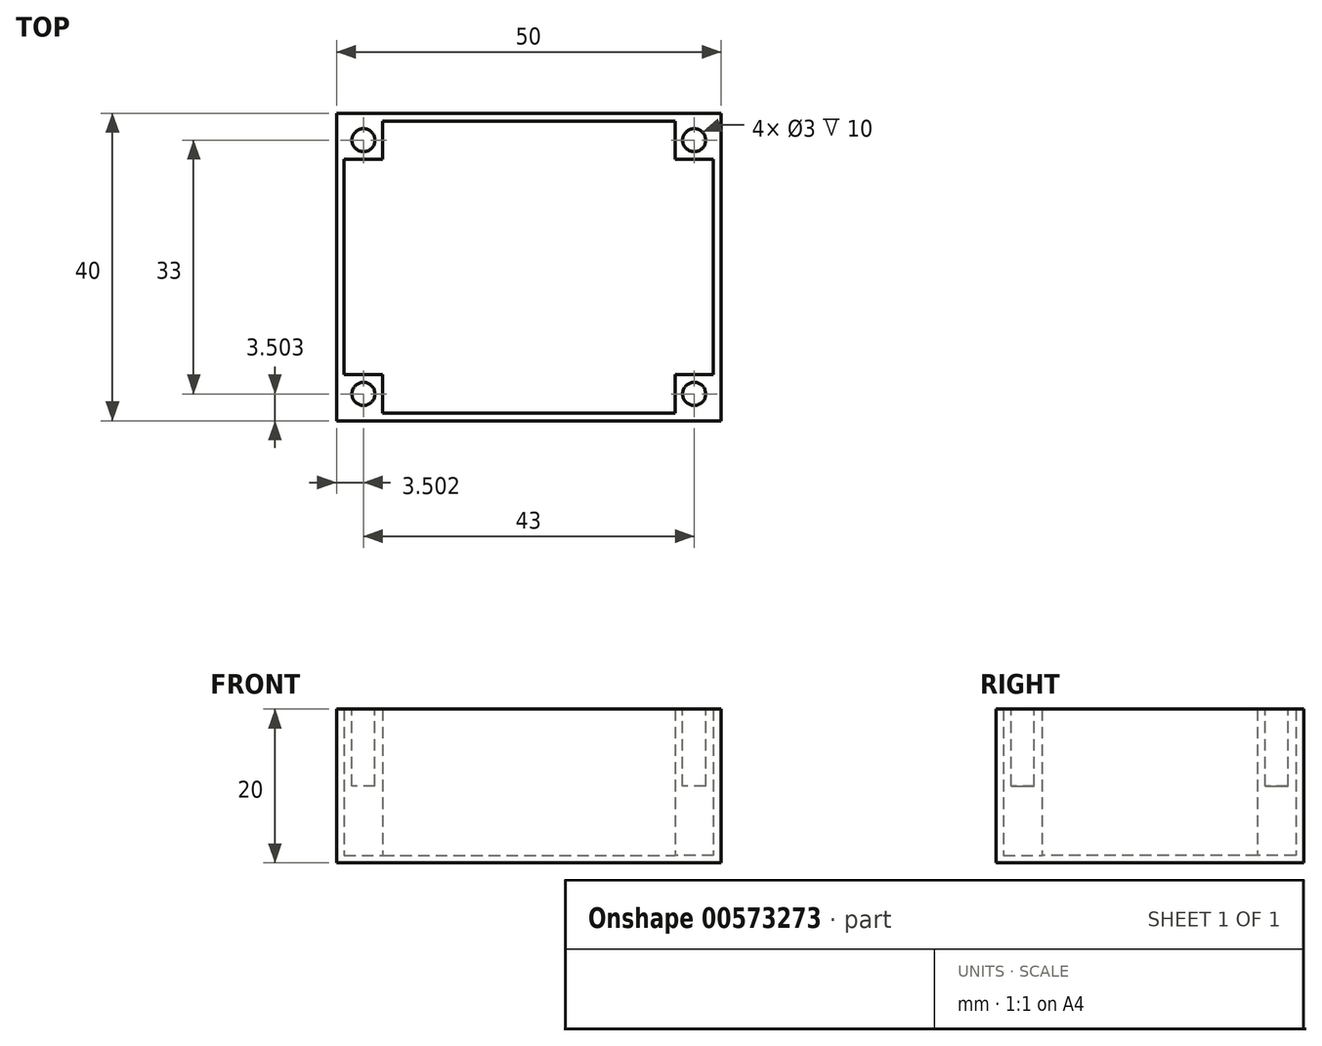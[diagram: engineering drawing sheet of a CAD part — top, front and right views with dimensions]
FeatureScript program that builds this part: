
annotation { "Feature Type Name" : "Feature", "Feature Type Description" : "" }
export const myFeature = defineFeature(function(context is Context, id is Id, definition is map)
    precondition{}
    {
        {
            var Q0;
            Q0=qCreatedBy(makeId("Top.planeOp"),FACE);
            var sketch = newSketch(context, id + "F0", { "sketchPlane" : qUnion([Q0])});
            skLineSegment(sketch, "E0.bottom", {"start": v(-61.69, 57.06) * mm, "end": v(-11.69, 57.06) * mm});
            skLineSegment(sketch, "E0.top", {"start": v(-61.69, 17.06) * mm, "end": v(-11.69, 17.06) * mm});
            skLineSegment(sketch, "E0.left", {"start": v(-61.69, 57.06) * mm, "end": v(-61.69, 17.06) * mm});
            skLineSegment(sketch, "E0.right", {"start": v(-11.69, 57.06) * mm, "end": v(-11.69, 17.06) * mm});
            skSolve(sketch);
        }
        {
            var Q0;
            Q0=makeQuery(id+"F0.imprint","IMPRINT",FACE,{"disambiguationData":[TD([[makeQuery(id+"F0.imprint","IMPRINT",EDGE,{"derivedFrom":sQuery(id+"F0.wireOp",EDGE,"E0.bottom")}),-1.0]])]});
            extrude(context, id + "F1", {"entities" : qUnion([Q0]), "depth" : 20 * mm, "offsetDistance" : 25 * mm});
        }
        {
            var Q0;
            Q0=makeQuery(id+"F1.opExtrude","CAP_FACE",FACE,{"disambiguationData":[OSD([sQuery(id+"F0.wireOp",EDGE,"E0.bottom"),sQuery(id+"F0.wireOp",EDGE,"E0.top"),sQuery(id+"F0.wireOp",EDGE,"E0.left"),sQuery(id+"F0.wireOp",EDGE,"E0.right")])],"isStart":false});
            var sketch = newSketch(context, id + "F2", { "sketchPlane" : qUnion([Q0])});
            skLineSegment(sketch, "E1.bottom", {"start": v(-60.69, 56.06) * mm, "end": v(-12.69, 56.06) * mm});
            skLineSegment(sketch, "E1.top", {"start": v(-60.69, 18.06) * mm, "end": v(-12.69, 18.06) * mm});
            skLineSegment(sketch, "E1.left", {"start": v(-60.69, 56.06) * mm, "end": v(-60.69, 18.06) * mm});
            skLineSegment(sketch, "E1.right", {"start": v(-12.69, 56.06) * mm, "end": v(-12.69, 18.06) * mm});
            skSolve(sketch);
        }
        {
            var Q0;
            Q0=makeQuery(id+"F2.imprint","IMPRINT",FACE,{"disambiguationData":[TD([[makeQuery(id+"F2.imprint","IMPRINT",EDGE,{"derivedFrom":sQuery(id+"F2.wireOp",EDGE,"E1.bottom")}),-1.0]])]});
            extrude(context, id + "F3", {"entities" : qUnion([Q0]), "operationType" : NewBodyOperationType.REMOVE, "oppositeDirection" : true, "depth" : 19 * mm, "offsetDistance" : 25 * mm});
        }
        {
            var Q0;
            Q0=makeQuery(id+"F3.boolean.opBoolean","COPY",FACE,{"derivedFrom":makeQuery(id+"F3.opExtrude","CAP_FACE",FACE,{"disambiguationData":[OSD([sQuery(id+"F2.wireOp",EDGE,"E1.bottom"),sQuery(id+"F2.wireOp",EDGE,"E1.top"),sQuery(id+"F2.wireOp",EDGE,"E1.left"),sQuery(id+"F2.wireOp",EDGE,"E1.right")])],"isStart":false})});
            var sketch = newSketch(context, id + "F4", { "sketchPlane" : qUnion([Q0])});
            skLineSegment(sketch, "E2.bottom", {"start": v(-12.69, 56.06) * mm, "end": v(-17.69, 56.06) * mm});
            skLineSegment(sketch, "E2.top", {"start": v(-12.69, 51.06) * mm, "end": v(-17.69, 51.06) * mm});
            skLineSegment(sketch, "E2.left", {"start": v(-12.69, 56.06) * mm, "end": v(-12.69, 51.06) * mm});
            skLineSegment(sketch, "E2.right", {"start": v(-17.69, 56.06) * mm, "end": v(-17.69, 51.06) * mm});
            skLineSegment(sketch, "E3.bottom", {"start": v(-12.69, 18.06) * mm, "end": v(-17.69, 18.06) * mm});
            skLineSegment(sketch, "E3.top", {"start": v(-12.69, 23.06) * mm, "end": v(-17.69, 23.06) * mm});
            skLineSegment(sketch, "E3.left", {"start": v(-12.69, 18.06) * mm, "end": v(-12.69, 23.06) * mm});
            skLineSegment(sketch, "E3.right", {"start": v(-17.69, 18.06) * mm, "end": v(-17.69, 23.06) * mm});
            skLineSegment(sketch, "E4.bottom", {"start": v(-60.69, 56.06) * mm, "end": v(-55.69, 56.06) * mm});
            skLineSegment(sketch, "E4.top", {"start": v(-60.69, 51.06) * mm, "end": v(-55.69, 51.06) * mm});
            skLineSegment(sketch, "E4.left", {"start": v(-60.69, 56.06) * mm, "end": v(-60.69, 51.06) * mm});
            skLineSegment(sketch, "E4.right", {"start": v(-55.69, 56.06) * mm, "end": v(-55.69, 51.06) * mm});
            skLineSegment(sketch, "E5.bottom", {"start": v(-60.69, 18.06) * mm, "end": v(-55.69, 18.06) * mm});
            skLineSegment(sketch, "E5.top", {"start": v(-60.69, 23.06) * mm, "end": v(-55.69, 23.06) * mm});
            skLineSegment(sketch, "E5.left", {"start": v(-60.69, 18.06) * mm, "end": v(-60.69, 23.06) * mm});
            skLineSegment(sketch, "E5.right", {"start": v(-55.69, 18.06) * mm, "end": v(-55.69, 23.06) * mm});
            skSolve(sketch);
        }
        {
            var Q0;
            Q0=makeQuery(id+"F4.imprint","IMPRINT",FACE,{"disambiguationData":[TD([[makeQuery(id+"F4.imprint","IMPRINT",EDGE,{"derivedFrom":sQuery(id+"F4.wireOp",EDGE,"E2.bottom")}),-1.0]])]});
            var Q1;
            Q1=makeQuery(id+"F4.imprint","IMPRINT",FACE,{"disambiguationData":[TD([[makeQuery(id+"F4.imprint","IMPRINT",EDGE,{"derivedFrom":sQuery(id+"F4.wireOp",EDGE,"E3.bottom")}),1.0]])]});
            var Q2;
            Q2=makeQuery(id+"F4.imprint","IMPRINT",FACE,{"disambiguationData":[TD([[makeQuery(id+"F4.imprint","IMPRINT",EDGE,{"derivedFrom":sQuery(id+"F4.wireOp",EDGE,"E5.bottom")}),1.0]])]});
            var Q3;
            Q3=makeQuery(id+"F4.imprint","IMPRINT",FACE,{"disambiguationData":[TD([[makeQuery(id+"F4.imprint","IMPRINT",EDGE,{"derivedFrom":sQuery(id+"F4.wireOp",EDGE,"E4.bottom")}),-1.0]])]});
            extrude(context, id + "F5", {"entities" : qUnion([Q0, Q1, Q2, Q3]), "operationType" : NewBodyOperationType.ADD, "depth" : 19 * mm, "offsetDistance" : 25 * mm});
        }
        {
            var Q0;
            Q0=makeQuery(id+"F5.boolean.opBoolean","MERGE",FACE,{"derivedFrom":[makeQuery(id+"F1.opExtrude","CAP_FACE",FACE,{"disambiguationData":[OSD([sQuery(id+"F0.wireOp",EDGE,"E0.bottom"),sQuery(id+"F0.wireOp",EDGE,"E0.top"),sQuery(id+"F0.wireOp",EDGE,"E0.left"),sQuery(id+"F0.wireOp",EDGE,"E0.right")])],"isStart":false}),makeQuery(id+"F5.opExtrude","CAP_FACE",FACE,{"disambiguationData":[OSD([sQuery(id+"F4.wireOp",EDGE,"E2.bottom"),sQuery(id+"F4.wireOp",EDGE,"E2.top"),sQuery(id+"F4.wireOp",EDGE,"E2.left"),sQuery(id+"F4.wireOp",EDGE,"E2.right")])],"isStart":false}),makeQuery(id+"F5.opExtrude","CAP_FACE",FACE,{"disambiguationData":[OSD([sQuery(id+"F4.wireOp",EDGE,"E3.bottom"),sQuery(id+"F4.wireOp",EDGE,"E3.top"),sQuery(id+"F4.wireOp",EDGE,"E3.left"),sQuery(id+"F4.wireOp",EDGE,"E3.right")])],"isStart":false}),makeQuery(id+"F5.opExtrude","CAP_FACE",FACE,{"disambiguationData":[OSD([sQuery(id+"F4.wireOp",EDGE,"E4.bottom"),sQuery(id+"F4.wireOp",EDGE,"E4.top"),sQuery(id+"F4.wireOp",EDGE,"E4.left"),sQuery(id+"F4.wireOp",EDGE,"E4.right")])],"isStart":false}),makeQuery(id+"F5.opExtrude","CAP_FACE",FACE,{"disambiguationData":[OSD([sQuery(id+"F4.wireOp",EDGE,"E5.bottom"),sQuery(id+"F4.wireOp",EDGE,"E5.top"),sQuery(id+"F4.wireOp",EDGE,"E5.left"),sQuery(id+"F4.wireOp",EDGE,"E5.right")])],"isStart":false})]});
            var sketch = newSketch(context, id + "F6", { "sketchPlane" : qUnion([Q0])});
            skCircle(sketch, "E6", {"center": v(-58.19, 53.56) * mm, "radius": 1.5 * mm});
            skPoint(sketch, "E6.centerSnap0", {"position": v(-58.19, 51.06) * mm});
            skPoint(sketch, "E6.centerSnap1", {"position": v(-55.69, 53.56) * mm});
            skCircle(sketch, "E7", {"center": v(-58.19, 20.56) * mm, "radius": 1.5 * mm});
            skPoint(sketch, "E7.centerSnap0", {"position": v(-55.69, 20.56) * mm});
            skPoint(sketch, "E7.centerSnap1", {"position": v(-58.19, 23.06) * mm});
            skCircle(sketch, "E8", {"center": v(-15.19, 20.56) * mm, "radius": 1.5 * mm});
            skPoint(sketch, "E8.centerSnap0", {"position": v(-15.19, 23.06) * mm});
            skPoint(sketch, "E8.centerSnap1", {"position": v(-17.69, 20.56) * mm});
            skCircle(sketch, "E9", {"center": v(-15.19, 53.56) * mm, "radius": 1.5 * mm});
            skPoint(sketch, "E9.centerSnap0", {"position": v(-17.69, 53.56) * mm});
            skPoint(sketch, "E9.centerSnap1", {"position": v(-15.19, 51.06) * mm});
            skSolve(sketch);
        }
        {
            var Q0;
            Q0=makeQuery(id+"F6.imprint","IMPRINT",FACE,{"disambiguationData":[TD([[makeQuery(id+"F6.imprint","IMPRINT",EDGE,{"derivedFrom":sQuery(id+"F6.wireOp",EDGE,"E9")}),1.0]])]});
            var Q1;
            Q1=makeQuery(id+"F6.imprint","IMPRINT",FACE,{"disambiguationData":[TD([[makeQuery(id+"F6.imprint","IMPRINT",EDGE,{"derivedFrom":sQuery(id+"F6.wireOp",EDGE,"E8")}),1.0]])]});
            var Q2;
            Q2=makeQuery(id+"F6.imprint","IMPRINT",FACE,{"disambiguationData":[TD([[makeQuery(id+"F6.imprint","IMPRINT",EDGE,{"derivedFrom":sQuery(id+"F6.wireOp",EDGE,"E7")}),1.0]])]});
            var Q3;
            Q3=makeQuery(id+"F6.imprint","IMPRINT",FACE,{"disambiguationData":[TD([[makeQuery(id+"F6.imprint","IMPRINT",EDGE,{"derivedFrom":sQuery(id+"F6.wireOp",EDGE,"E6")}),1.0]])]});
            extrude(context, id + "F7", {"entities" : qUnion([Q0, Q1, Q2, Q3]), "operationType" : NewBodyOperationType.REMOVE, "oppositeDirection" : true, "depth" : 10 * mm, "offsetDistance" : 25 * mm});
        }
    });
